# Revit family: Electronics_Desono_Biamp_Two-Way-Surface-Mount-Loudspeaker_KUBO5_KUBO5T
name_source: partatom
category: Communication Devices
units: mm (PartAtom-declared; Revit-internal decimal feet)

## family parameters
Cut with Voids When Loaded = No
Host = Face
Maintain Annotation Orientation = No
OmniClass Number = 23.85.10.11.14.14.14
Part Type = Normal
Room Calculation Point = No
Round Connector Dimension = Use Diameter
Shared = No

## types (4) — shared parameters
Default Elevation = 4' - 0"
Depth = 0' - 5 1/2"
Environmental = IP40 per IEC 60529
Height = 0' - 6"
Input Connection = (2x) 2-way Euroblock connectors for daisy-chaining;connectors accept up to 12 AWG (2.5 mm²)conductors
Manufacturer = Biamp
Mounting Provisions = U-bracket
Operating Environment = Indoor
Operating Mode = Passive
Product Documentation Link = https://downloads.biamp.com
Product Page URL = https://www.biamp.com
Product data url = https://www.bimobject.com
Protection = 3-step self-resetting protection
Transducers = LF 1 x 5.25 (133 mm) coated paper cone; HF 1 x 1 (25 mm) soft dome
URL = https://www.biamp.com
Width = 0' - 6 1/2"

## per-type parameters (varying)
| type | Bracket Material | Connector Description | Continuous Power Handling Nominal Impedance | Controls | Description | Grill Material | Housing Material | Nominal Beamwidth  (H x V) | Nominal Maximum SPL @ 1m | Nominal Sensitivity @ 1m | Operating Range (-10dB) | Recommended Amplifers | Transformer | Weight |
| KUBO5 B | Biamp - Metal - Black | 2-way Euroblock; 20V 50W 8Ω (200W peak) | 20V; 50W @ 8Ω (200W peak) |  | Desono™ KUBO5 Two-Way 5.25-Inch Surface Mount Loudspeaker | Biamp - Plastic - Black(Grid) | Biamp - Plastic - Black | 70° x 70° | Peak - 107dB; Continuous - 101dB | 1W - 84dB; 2.83V - 84dB | 115 Hz to 20 kHz | 50W - 100W @ 8Ω (20V - 28V) |  | 3.75 lb |
| KUBO5 W | Biamp - Metal - White | 2-way Euroblock; 20V 50W 8Ω (200W peak) | 20V; 50W @ 8Ω (200W peak) |  | Desono™ KUBO5 Two-Way 5.25-Inch Surface Mount Loudspeaker | Biamp - Plastic - White(Grid) | Biamp - Plastic - White | 70° x 70° | Peak - 107dB; Continuous - 101dB | 1W - 84dB; 2.83V - 84dB | 115 Hz to 20 kHz | 50W - 100W @ 8Ω (20V - 28V) |  | 3.75 lb |
| KUBO5T W | Biamp - Metal - White | 2-way Euroblock; Low impedance 16 ohms, 70V/100V operation | 28V; 50W @ 16Ω (200W peak) | Power tap / low impedance selector switch | Desono™ KUBO5T Two-Way 5.25-Inch Surface Mount Loudspeaker | Biamp - Plastic - White(Grid) | Biamp - Plastic - White | 80° x 80° | Peak - 110dB; Continuous - 104dB | 1W - 87dB; 2.83V - 84dB | 94 Hz to 20 kHz | 50W - 100W @ 16Ω (28V - 40V) | 70V: 10W, 5W, 2.5W, 1.25W;100V: 10W, 5W, 2.5W | 4.41 lb |
| KUBO5T B | Biamp - Metal - Black | 2-way Euroblock; Low impedance 16 ohms, 70V/100V operation | 28V; 50W @ 16Ω (200W peak) | Power tap / low impedance selector switch | Desono™ KUBO5T Two-Way 5.25-Inch Surface Mount Loudspeaker | Biamp - Plastic - Black(Grid) | Biamp - Plastic - Black | 80° x 80° | Peak - 110dB; Continuous - 104dB | 1W - 87dB; 2.83V - 84dB | 94 Hz to 20 kHz | 50W - 100W @ 16Ω (28V - 40V) | 70V: 10W, 5W, 2.5W, 1.25W;100V: 10W, 5W, 2.5W | 4.41 lb |

note: column(s) folded — value = type name in every type: Model

## geometry (parser evidence)
native form markers: Sweep x5
no freeform markers — native parametric forms only
